FREECAD ASSEMBLY — COMPONENT RECIPES ("Assembly")

This assembly document has 4 components, labeled P0..P3 below (a component is one placed body or linked part). 4 of them carry a construction recipe — the FreeCAD feature program that regenerates the part from scratch, quoted from this document or its linked companion documents; the rest are supplied as boundary geometry only. No exploded tour is included for this assembly.
COMPONENT P0 — recipe-attached ("Link", a linked part whose construction recipe lives in a companion FreeCAD document of the same project; that document's serialized recipe follows).
Construction recipe (the companion document, serialized — sketch geometry with constraints, then the solid features built on it; lengths are millimeters unless a unit is written):

FCSTD DOCUMENT  (FreeCAD 1.0R39319 (Git))
Label: Base-Bracket
License: All rights reserved
LicenseURL: https://en.wikipedia.org/wiki/All_rights_reserved
objects: Sketcher::SketchObject×5, PartDesign::Pad×4, PartDesign::Body×3, PartDesign::Pocket×1
note: 28 computed .brp shape members not serialized (recipe doc carries the construction recipe); baked Part::Feature solids carry a one-line shape summary decoded from their .brp

FEATURE [Sketcher::SketchObject] Sketch
  ArcFitTolerance = 1e-06
  AttachmentSupport = -> [XY_Plane]
  FullyConstrained = true
  MakeInternals = false
  MapMode = 5
  sketch-geometry (14):
    g0: LineSegment StartX=-52.5 StartY=13 StartZ=0 EndX=-52.5 EndY=-13 EndZ=0
    g1: LineSegment StartX=-40.5 StartY=-25 StartZ=0 EndX=40.5 EndY=-25 EndZ=0
    g2: LineSegment StartX=52.5 StartY=-13 StartZ=0 EndX=52.5 EndY=13 EndZ=0
    g3: LineSegment StartX=40.5 StartY=25 StartZ=0 EndX=-40.5 EndY=25 EndZ=0
    g4: ArcOfCircle CenterX=-40.5 CenterY=13 CenterZ=0 NormalX=0 NormalY=0 NormalZ=1 AngleXU=0 Radius=12 StartAngle=1.5708 EndAngle=3.14159
    g5: ArcOfCircle CenterX=-40.5 CenterY=-13 CenterZ=0 NormalX=0 NormalY=0 NormalZ=1 AngleXU=0 Radius=12 StartAngle=3.14159 EndAngle=4.71239
    g6: ArcOfCircle CenterX=40.5 CenterY=-13 CenterZ=0 NormalX=0 NormalY=0 NormalZ=1 AngleXU=0 Radius=12 StartAngle=4.71239 EndAngle=6.28319
    g7: ArcOfCircle CenterX=40.5 CenterY=13 CenterZ=0 NormalX=0 NormalY=0 NormalZ=1 AngleXU=0 Radius=12 StartAngle=0 EndAngle=1.5708
    g8: GeomPoint [constr] X=-52.5 Y=25 Z=0
    g9: GeomPoint [constr] X=52.5 Y=-25 Z=0
    g10: Circle CenterX=-40.5 CenterY=13 CenterZ=0 NormalX=0 NormalY=0 NormalZ=1 AngleXU=0 Radius=4
    g11: Circle CenterX=-40.5 CenterY=-13 CenterZ=0 NormalX=0 NormalY=0 NormalZ=1 AngleXU=0 Radius=4
    g12: Circle CenterX=40.5 CenterY=13 CenterZ=0 NormalX=0 NormalY=0 NormalZ=1 AngleXU=0 Radius=4
    g13: Circle CenterX=40.5 CenterY=-13 CenterZ=0 NormalX=0 NormalY=0 NormalZ=1 AngleXU=0 Radius=4
  constraints (31):
    c: Tangent(g0,g4) = -1.5708
    c: Tangent(g0,g5) = -1.5708
    c: Tangent(g1,g5) = -1.5708
    c: Tangent(g1,g6) = -1.5708
    c: Tangent(g2,g6) = -1.5708
    c: Tangent(g2,g7) = -1.5708
    c: Tangent(g3,g7) = -1.5708
    c: Tangent(g3,g4) = -1.5708
    c: Vertical(g0)
    c: Vertical(g2)
    c: Horizontal(g1)
    c: Horizontal(g3)
    c: Equal(g4,g5)
    c: Equal(g5,g6)
    c: Equal(g6,g7)
    c: PointOnObject(g8,g0)
    c: PointOnObject(g8,g3)
    c: PointOnObject(g9,g1)
    c: PointOnObject(g9,g2)
    c: Symmetric(g4,g6,g-1)
    c: Distance(g1,g3) = 50
    c: Radius(g7) = 12
    c: Distance(g2,g0) = 105
    c: Diameter(g10) = 8
    c: Coincident(g10,g4)
    c: Diameter(g11) = 8
    c: Block(g11)
    c: Diameter(g12) = 8
    c: Diameter(g13) = 8
    c: Block(g13)
    c: Block(g12)
FEATURE [PartDesign::Pad] Pad
  Direction = (0,0,1)
  Length = 10
  Length2 = 10
  Profile = -> Sketch
  ReferenceAxis = -> Sketch [N_Axis]
  Refine = true
  Suppressed = false
  Type = 0
FEATURE [Sketcher::SketchObject] Sketch001
  ArcFitTolerance = 1e-06
  AttachmentSupport = -> [Pad]
  ExternalGeometry = -> [Pad]
  FullyConstrained = true
  MakeInternals = false
  MapMode = 5
  Placement = pos=(0,0,10) rot=(0,0,1;0rad)
  sketch-geometry (4):
    g0: LineSegment StartX=-27.5 StartY=25 StartZ=0 EndX=-27.5 EndY=-25 EndZ=0
    g1: LineSegment StartX=-27.5 StartY=-25 StartZ=0 EndX=27.5 EndY=-25 EndZ=0
    g2: LineSegment StartX=27.5 StartY=-25 StartZ=0 EndX=27.5 EndY=25 EndZ=0
    g3: LineSegment StartX=27.5 StartY=25 StartZ=0 EndX=-27.5 EndY=25 EndZ=0
  constraints (11):
    c: Coincident(g0,g1)
    c: Coincident(g1,g2)
    c: Coincident(g2,g3)
    c: Coincident(g3,g0)
    c: Vertical(g0)
    c: Vertical(g2)
    c: Horizontal(g1)
    c: Horizontal(g3)
    c: Symmetric(g0,g1,g-1)
    c: PointOnObject(g0,g-3)
    c: Distance(g2,g0) = 55
FEATURE [PartDesign::Pocket] Pocket
  BaseFeature = -> Pad
  Direction = (0,0,-1)
  Length = 5
  Length2 = 5
  Profile = -> Sketch001
  ReferenceAxis = -> Sketch001 [N_Axis]
  Refine = true
  Suppressed = false
  Type = 0
FEATURE [PartDesign::Body] Body  label="Base"
  AllowCompound = false
  Group = -> [Sketch,Pad,Sketch001,Pocket]
  Origin = -> Origin
  Tip = -> Pocket
FEATURE [Sketcher::SketchObject] Sketch002
  ArcFitTolerance = 1e-06
  AttachmentSupport = -> [XY_Plane001]
  FullyConstrained = true
  MakeInternals = false
  MapMode = 5
  sketch-geometry (10):
    g0: LineSegment StartX=-25 StartY=13 StartZ=0 EndX=-25 EndY=0 EndZ=0
    g1: LineSegment StartX=-25 StartY=0 StartZ=0 EndX=25 EndY=0 EndZ=0
    g2: LineSegment StartX=25 StartY=0 StartZ=0 EndX=25 EndY=13 EndZ=0
    g3: LineSegment StartX=13 StartY=25 StartZ=0 EndX=-13 EndY=25 EndZ=0
    g4: ArcOfCircle CenterX=-13 CenterY=13 CenterZ=0 NormalX=0 NormalY=0 NormalZ=1 AngleXU=0 Radius=12 StartAngle=1.5708 EndAngle=3.14159
    g5: GeomPoint [constr] X=-25 Y=25 Z=0
    g6: ArcOfCircle CenterX=13 CenterY=13 CenterZ=0 NormalX=0 NormalY=0 NormalZ=1 AngleXU=0 Radius=12 StartAngle=0 EndAngle=1.5708
    g7: GeomPoint [constr] X=25 Y=25 Z=0
    g8: Circle CenterX=13 CenterY=13 CenterZ=0 NormalX=0 NormalY=0 NormalZ=1 AngleXU=0 Radius=4
    g9: Circle CenterX=-13 CenterY=13 CenterZ=0 NormalX=0 NormalY=0 NormalZ=1 AngleXU=0 Radius=4
  constraints (23):
    c: Coincident(g0,g1)
    c: Coincident(g1,g2)
    c: Vertical(g0)
    c: Vertical(g2)
    c: Horizontal(g1)
    c: Horizontal(g3)
    c: PointOnObject(g1,g-1)
    c: PointOnObject(g5,g0)
    c: PointOnObject(g5,g3)
    c: Tangent(g0,g4) = -1.5708
    c: Tangent(g3,g4) = -1.5708
    c: PointOnObject(g7,g3)
    c: PointOnObject(g7,g2)
    c: Tangent(g3,g6) = -1.5708
    c: Tangent(g2,g6) = -1.5708
    c: Distance(g2,g0) = 50
    c: Distance(g1,g3) = 25
    c: Radius(g6) = 12
    c: Symmetric(g4,g6,g-2)
    c: Diameter(g8) = 8
    c: Coincident(g8,g6)
    c: Diameter(g9) = 8
    c: Block(g9)
FEATURE [PartDesign::Pad] Pad001
  Direction = (0,0,1)
  Length = 10
  Length2 = 10
  Profile = -> Sketch002
  ReferenceAxis = -> Sketch002 [N_Axis]
  Refine = true
  Suppressed = false
  Type = 0
FEATURE [Sketcher::SketchObject] Sketch003
  ArcFitTolerance = 1e-06
  AttachmentSupport = -> [Pad001]
  ExternalGeometry = -> [Pad001]
  FullyConstrained = true
  MakeInternals = false
  MapMode = 5
  Placement = pos=(0,0,0) rot=(1,0,0;1.5708rad)
  sketch-geometry (5):
    g0: ArcOfCircle CenterX=-63.5588 CenterY=50 CenterZ=0 NormalX=0 NormalY=0 NormalZ=1 AngleXU=0 Radius=55.5588 StartAngle=5.47944 EndAngle=6.28319
    g1: ArcOfCircle CenterX=0 CenterY=50 CenterZ=0 NormalX=0 NormalY=0 NormalZ=1 AngleXU=0 Radius=8 StartAngle=0 EndAngle=3.14159
    g2: ArcOfCircle CenterX=63.5588 CenterY=50 CenterZ=0 NormalX=0 NormalY=0 NormalZ=1 AngleXU=0 Radius=55.5588 StartAngle=3.14159 EndAngle=3.94533
    g3: Circle CenterX=0 CenterY=50 CenterZ=0 NormalX=0 NormalY=0 NormalZ=1 AngleXU=0 Radius=2.5
    g4: LineSegment StartX=-25 StartY=10 StartZ=0 EndX=25 EndY=10 EndZ=0
  constraints (13):
    c: Tangent(g0,g1) = 1.5708
    c: Tangent(g1,g2) = 1.5708
    c: Coincident(g2,g-3)
    c: Coincident(g-3,g0)
    c: Horizontal(g0,g1)
    c: PointOnObject(g1,g-2)
    c: Horizontal(g0,g1)
    c: DistanceY(g-1,g1) = 50
    c: Radius(g1) = 8
    c: Diameter(g3) = 5
    c: Coincident(g3,g1)
    c: Coincident(g4,g0)
    c: Coincident(g4,g2)
FEATURE [PartDesign::Pad] Pad002
  BaseFeature = -> Pad001
  Direction = (0,-1,2e-16)
  Length = 5
  Length2 = 10
  Profile = -> Sketch003
  ReferenceAxis = -> Sketch003 [N_Axis]
  Refine = true
  Reversed = true
  Suppressed = false
  Type = 0
FEATURE [PartDesign::Body] Body001  label="Bracket"
  AllowCompound = false
  Group = -> [Sketch002,Pad001,Sketch003,Pad002]
  Origin = -> Origin001
  Placement = pos=(26.0989,2.26605,52) rot=(0,0,-1;2.96706rad)
  Tip = -> Pad002
FEATURE [Sketcher::SketchObject] Sketch004
  ArcFitTolerance = 1e-06
  AttachmentSupport = -> [XY_Plane002]
  FullyConstrained = true
  MakeInternals = false
  MapMode = 5
  sketch-geometry (6):
    g0: ArcOfCircle CenterX=2.1316e-12 CenterY=50 CenterZ=0 NormalX=0 NormalY=0 NormalZ=1 AngleXU=0 Radius=8 StartAngle=-2.24e-12 EndAngle=3.14159
    g1: ArcOfCircle CenterX=-2.1314e-12 CenterY=-50 CenterZ=0 NormalX=0 NormalY=0 NormalZ=1 AngleXU=0 Radius=8 StartAngle=3.14159 EndAngle=6.28319
    g2: LineSegment StartX=8 StartY=50 StartZ=0 EndX=8 EndY=-50 EndZ=0
    g3: LineSegment StartX=-8 StartY=50 StartZ=0 EndX=-8 EndY=-50 EndZ=0
    g4: Circle CenterX=2.1316e-12 CenterY=50 CenterZ=0 NormalX=0 NormalY=0 NormalZ=1 AngleXU=0 Radius=2.5
    g5: Circle CenterX=2.1316e-12 CenterY=-50 CenterZ=0 NormalX=0 NormalY=0 NormalZ=1 AngleXU=0 Radius=2.5
  constraints (13):
    c: Tangent(g0,g2) = 1.5708
    c: Tangent(g0,g3) = -1.5708
    c: Tangent(g1,g2) = 1.5708
    c: Tangent(g1,g3) = -1.5708
    c: Equal(g0,g1)
    c: Vertical(g3)
    c: Coincident(g4,g0)
    c: Diameter(g4) = 5
    c: Radius(g0) = 8
    c: Symmetric(g0,g1,g-1)
    c: DistanceY(g-1,g0) = 50
    c: Diameter(g5) = 5
    c: Block(g5)
FEATURE [PartDesign::Pad] Pad003
  Direction = (0,0,1)
  Length = 2
  Length2 = 10
  Profile = -> Sketch004
  ReferenceAxis = -> Sketch004 [N_Axis]
  Refine = true
  Suppressed = false
  Type = 0
FEATURE [PartDesign::Body] Body002  label="Link"
  AllowCompound = false
  Group = -> [Sketch004,Pad003]
  Origin = -> Origin002
  Placement = pos=(-39,0,52) rot=(0,0,1;0rad)
  Tip = -> Pad003
COMPONENT P1 — same part as P0; its construction recipe is shown at P0.
COMPONENT P2 — same part as P0; its construction recipe is shown at P0.
COMPONENT P3 — same part as P0; its construction recipe is shown at P0.
PROVENANCE & LICENSES
A FreeCAD (.FCStd) document from a public repository crawl; recipes are the document's own serialized feature recipes (and, for linked parts, companion documents' recipes).
License: as declared in the source repository (recorded in the dataset sidecar).
